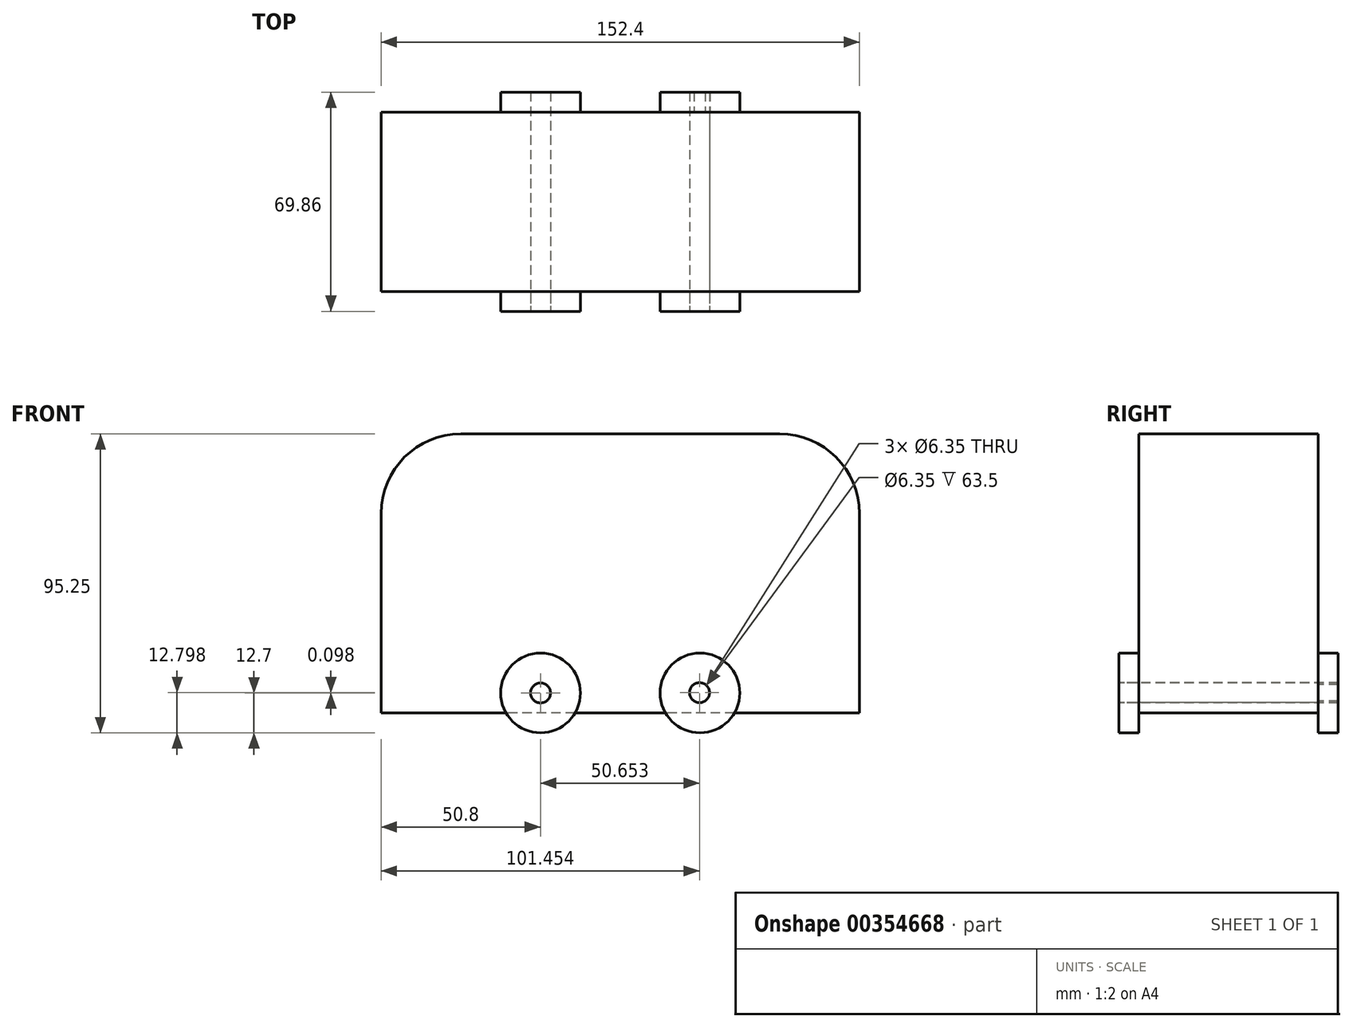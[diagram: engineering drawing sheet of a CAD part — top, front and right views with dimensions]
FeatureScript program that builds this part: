
annotation { "Feature Type Name" : "Feature", "Feature Type Description" : "" }
export const myFeature = defineFeature(function(context is Context, id is Id, definition is map)
    precondition{}
    {
        {
            var Q0;
            Q0=qCreatedBy(makeId("Front.planeOp"),FACE);
            var sketch = newSketch(context, id + "F0", { "sketchPlane" : qUnion([Q0])});
            skLineSegment(sketch, "E0.bottom", {"start": v(76.2, -44.45) * mm, "end": v(-76.2, -44.45) * mm});
            skLineSegment(sketch, "E0.top", {"start": v(50.8, 44.45) * mm, "end": v(-50.8, 44.45) * mm});
            skLineSegment(sketch, "E0.left", {"start": v(76.2, -44.45) * mm, "end": v(76.2, 19.05) * mm});
            skLineSegment(sketch, "E0.right", {"start": v(-76.2, -44.45) * mm, "end": v(-76.2, 19.05) * mm});
            skPoint(sketch, "E0.middle", {"position": v(0, 0) * mm});
            skPoint(sketch, "E1.visualSharp", {"position": v(-76.2, 44.45) * mm});
            skArc(sketch, "E1.filletArc", {"start": v(-50.8, 44.45) * mm, "mid": v(-68.76, 37.01) * mm, "end": v(-76.2, 19.05) * mm});
            skPoint(sketch, "E2.visualSharp", {"position": v(76.2, 44.45) * mm});
            skArc(sketch, "E2.filletArc", {"start": v(76.2, 19.05) * mm, "mid": v(68.76, 37.01) * mm, "end": v(50.8, 44.45) * mm});
            skSolve(sketch);
        }
        {
            var Q0;
            Q0=makeQuery(id+"F0.imprint","IMPRINT",FACE,{"disambiguationData":[TD([[makeQuery(id+"F0.imprint","IMPRINT",EDGE,{"derivedFrom":sQuery(id+"F0.wireOp",EDGE,"E0.bottom")}),-1.0]])]});
            extrude(context, id + "F1", {"entities" : qUnion([Q0]), "endBound" : BoundingType.SYMMETRIC, "depth" : 57.15 * mm});
        }
        {
            var Q0;
            Q0=makeQuery(id+"F1.opExtrude","CAP_FACE",FACE,{"disambiguationData":[OSD([sQuery(id+"F0.wireOp",EDGE,"E0.bottom"),sQuery(id+"F0.wireOp",EDGE,"E0.top"),sQuery(id+"F0.wireOp",EDGE,"E0.left"),sQuery(id+"F0.wireOp",EDGE,"E0.right")])],"isStart":false});
            var sketch = newSketch(context, id + "F2", { "sketchPlane" : qUnion([Q0])});
            skCircle(sketch, "E3", {"center": v(25.4, -38.1) * mm, "radius": 12.7 * mm});
            skCircle(sketch, "E4", {"center": v(-25.4, -38.1) * mm, "radius": 12.7 * mm});
            skSolve(sketch);
        }
        {
            var Q0;
            {var subQ0=sQuery(id+"F2.wireOp",EDGE,"E4");var subQ1=makeQuery(id+"F1.opExtrude","CAP_EDGE",EDGE,{"disambiguationData":[OSD([sQuery(id+"F0.wireOp",EDGE,"E0.bottom")])],"isStart":false});var subQ2=makeQuery(id+"F2.imprint","INTERSECT",VERTEX,{"disambiguationData":[OD(0.0)],"derivedFrom":[subQ1,subQ0]});Q0=makeQuery(id+"F2.imprint","IMPRINT",FACE,{"disambiguationData":[TD([[makeQuery(id+"F2.imprint","IMPRINT",EDGE,{"disambiguationData":[TD([[subQ2,1.0]])],"derivedFrom":subQ0}),1.0]])]});}
            var Q1;
            {var subQ0=sQuery(id+"F2.wireOp",EDGE,"E3");var subQ1=makeQuery(id+"F1.opExtrude","CAP_EDGE",EDGE,{"disambiguationData":[OSD([sQuery(id+"F0.wireOp",EDGE,"E0.bottom")])],"isStart":false});var subQ2=makeQuery(id+"F2.imprint","INTERSECT",VERTEX,{"disambiguationData":[OD(0.0)],"derivedFrom":[subQ1,subQ0]});Q1=makeQuery(id+"F2.imprint","IMPRINT",FACE,{"disambiguationData":[TD([[makeQuery(id+"F2.imprint","IMPRINT",EDGE,{"disambiguationData":[TD([[subQ2,-1.0]])],"derivedFrom":subQ0}),1.0]])]});}
            var Q2;
            {var subQ0=sQuery(id+"F2.wireOp",EDGE,"E4");var subQ1=makeQuery(id+"F1.opExtrude","CAP_EDGE",EDGE,{"disambiguationData":[OSD([sQuery(id+"F0.wireOp",EDGE,"E0.bottom")])],"isStart":false});var subQ2=makeQuery(id+"F2.imprint","INTERSECT",VERTEX,{"disambiguationData":[OD(0.0)],"derivedFrom":[subQ1,subQ0]});Q2=makeQuery(id+"F2.imprint","IMPRINT",FACE,{"disambiguationData":[TD([[makeQuery(id+"F2.imprint","IMPRINT",EDGE,{"disambiguationData":[TD([[subQ2,-1.0]])],"derivedFrom":subQ0}),1.0]])]});}
            var Q3;
            {var subQ0=sQuery(id+"F2.wireOp",EDGE,"E3");var subQ1=makeQuery(id+"F1.opExtrude","CAP_EDGE",EDGE,{"disambiguationData":[OSD([sQuery(id+"F0.wireOp",EDGE,"E0.bottom")])],"isStart":false});var subQ2=makeQuery(id+"F2.imprint","INTERSECT",VERTEX,{"disambiguationData":[OD(0.0)],"derivedFrom":[subQ1,subQ0]});Q3=makeQuery(id+"F2.imprint","IMPRINT",FACE,{"disambiguationData":[TD([[makeQuery(id+"F2.imprint","IMPRINT",EDGE,{"disambiguationData":[TD([[subQ2,1.0]])],"derivedFrom":subQ0}),1.0]])]});}
            var Q4;
            Q4=sQuery(id+"F2.wireOp",EDGE,"E3");
            var Q5;
            Q5=sQuery(id+"F2.wireOp",EDGE,"E4");
            extrude(context, id + "F3", {"entities" : qUnion([Q0, Q1, Q2, Q3]), "surfaceEntities" : qUnion([Q4, Q5]), "depth" : 6.35 * mm});
        }
        {
            var Q0;
            Q0=makeQuery(id+"F1.opExtrude","CAP_FACE",FACE,{"disambiguationData":[OSD([sQuery(id+"F0.wireOp",EDGE,"E0.bottom"),sQuery(id+"F0.wireOp",EDGE,"E0.top"),sQuery(id+"F0.wireOp",EDGE,"E0.left"),sQuery(id+"F0.wireOp",EDGE,"E0.right")])],"isStart":true});
            var sketch = newSketch(context, id + "F4", { "sketchPlane" : qUnion([Q0])});
            skCircle(sketch, "E5", {"center": v(-25.4, -38.1) * mm, "radius": 12.7 * mm});
            skCircle(sketch, "E6", {"center": v(25.4, -38.1) * mm, "radius": 12.7 * mm});
            skCircle(sketch, "E7", {"center": v(25.4, -38.1) * mm, "radius": 3.18 * mm});
            skCircle(sketch, "E8", {"center": v(-25.4, -38.1) * mm, "radius": 3.18 * mm});
            skSolve(sketch);
        }
        {
            var Q0;
            {var subQ0=sQuery(id+"F4.wireOp",EDGE,"E5");var subQ1=makeQuery(id+"F1.opExtrude","CAP_EDGE",EDGE,{"disambiguationData":[OSD([sQuery(id+"F0.wireOp",EDGE,"E0.bottom")])],"isStart":true});var subQ2=makeQuery(id+"F4.imprint","INTERSECT",VERTEX,{"disambiguationData":[OD(0.0)],"derivedFrom":[subQ1,subQ0]});Q0=makeQuery(id+"F4.imprint","IMPRINT",FACE,{"disambiguationData":[TD([[makeQuery(id+"F4.imprint","IMPRINT",EDGE,{"disambiguationData":[TD([[subQ2,-1.0]])],"derivedFrom":subQ0}),1.0]])]});}
            var Q1;
            {var subQ0=sQuery(id+"F4.wireOp",EDGE,"E6");var subQ1=makeQuery(id+"F1.opExtrude","CAP_EDGE",EDGE,{"disambiguationData":[OSD([sQuery(id+"F0.wireOp",EDGE,"E0.bottom")])],"isStart":true});var subQ2=makeQuery(id+"F4.imprint","INTERSECT",VERTEX,{"disambiguationData":[OD(0.0)],"derivedFrom":[subQ1,subQ0]});Q1=makeQuery(id+"F4.imprint","IMPRINT",FACE,{"disambiguationData":[TD([[makeQuery(id+"F4.imprint","IMPRINT",EDGE,{"disambiguationData":[TD([[subQ2,1.0]])],"derivedFrom":subQ0}),1.0]])]});}
            var Q2;
            {var subQ0=sQuery(id+"F4.wireOp",EDGE,"E6");var subQ1=makeQuery(id+"F1.opExtrude","CAP_EDGE",EDGE,{"disambiguationData":[OSD([sQuery(id+"F0.wireOp",EDGE,"E0.bottom")])],"isStart":true});var subQ2=makeQuery(id+"F4.imprint","INTERSECT",VERTEX,{"disambiguationData":[OD(0.0)],"derivedFrom":[subQ1,subQ0]});Q2=makeQuery(id+"F4.imprint","IMPRINT",FACE,{"disambiguationData":[TD([[makeQuery(id+"F4.imprint","IMPRINT",EDGE,{"disambiguationData":[TD([[subQ2,-1.0]])],"derivedFrom":subQ0}),1.0]])]});}
            var Q3;
            {var subQ0=sQuery(id+"F4.wireOp",EDGE,"E5");var subQ1=makeQuery(id+"F1.opExtrude","CAP_EDGE",EDGE,{"disambiguationData":[OSD([sQuery(id+"F0.wireOp",EDGE,"E0.bottom")])],"isStart":true});var subQ2=makeQuery(id+"F4.imprint","INTERSECT",VERTEX,{"disambiguationData":[OD(0.0)],"derivedFrom":[subQ1,subQ0]});Q3=makeQuery(id+"F4.imprint","IMPRINT",FACE,{"disambiguationData":[TD([[makeQuery(id+"F4.imprint","IMPRINT",EDGE,{"disambiguationData":[TD([[subQ2,1.0]])],"derivedFrom":subQ0}),1.0]])]});}
            var Q4;
            Q4 = qSketchRegion(id + "F6", true);
            extrude(context, id + "F5", {"entities" : qUnion([Q0, Q1, Q2, Q3, Q4]), "operationType" : NewBodyOperationType.ADD, "depth" : 6.35 * mm});
        }
        {
            var Q0;
            Q0=makeQuery(id+"F3.opExtrude","CAP_FACE",FACE,{"disambiguationData":[OSD([sQuery(id+"F2.wireOp",EDGE,"E4")])],"isStart":false});
            var sketch = newSketch(context, id + "F6", { "sketchPlane" : qUnion([Q0])});
            skCircle(sketch, "E9", {"center": v(-25.4, -38.1) * mm, "radius": 3.18 * mm});
            skCircle(sketch, "E10", {"center": v(25.25, -38) * mm, "radius": 3.18 * mm});
            skSolve(sketch);
        }
        {
            var Q0;
            Q0=makeQuery(id+"F6.imprint","IMPRINT",FACE,{"disambiguationData":[TD([[makeQuery(id+"F6.imprint","IMPRINT",EDGE,{"derivedFrom":sQuery(id+"F6.wireOp",EDGE,"E9")}),1.0]])]});
            var Q1;
            Q1=makeQuery(id+"F6.imprint","IMPRINT",FACE,{"disambiguationData":[TD([[makeQuery(id+"F6.imprint","IMPRINT",EDGE,{"derivedFrom":sQuery(id+"F6.wireOp",EDGE,"E10")}),1.0]])]});
            var Q2;
            Q2=makeQuery(id+"F4.imprint","IMPRINT",FACE,{"disambiguationData":[TD([[makeQuery(id+"F4.imprint","IMPRINT",EDGE,{"derivedFrom":sQuery(id+"F4.wireOp",EDGE,"E8")}),1.0]])]});
            var Q3;
            Q3=makeQuery(id+"F4.imprint","IMPRINT",FACE,{"disambiguationData":[TD([[makeQuery(id+"F4.imprint","IMPRINT",EDGE,{"derivedFrom":sQuery(id+"F4.wireOp",EDGE,"E7")}),1.0]])]});
            var Q4;
            Q4=makeQuery(id+"F5.opExtrude","CAP_FACE",FACE,{"disambiguationData":[OSD([sQuery(id+"F4.wireOp",EDGE,"E6"),sQuery(id+"F4.wireOp",EDGE,"E7")])],"isStart":false});
            var Q5;
            Q5=makeQuery(id+"F5.opExtrude","CAP_FACE",FACE,{"disambiguationData":[OSD([sQuery(id+"F4.wireOp",EDGE,"E5"),sQuery(id+"F4.wireOp",EDGE,"E8")])],"isStart":false});
            extrude(context, id + "F7", {"entities" : qUnion([Q0, Q1, Q2, Q3, Q4, Q5]), "operationType" : NewBodyOperationType.REMOVE, "endBound" : BoundingType.THROUGH_ALL, "oppositeDirection" : true, "depth" : 25.4 * mm});
        }
        {
            var Q0;
            Q0=makeQuery(id+"F6.imprint","IMPRINT",FACE,{"disambiguationData":[TD([[makeQuery(id+"F6.imprint","IMPRINT",EDGE,{"derivedFrom":sQuery(id+"F6.wireOp",EDGE,"E9")}),1.0]])]});
            var Q1;
            Q1=makeQuery(id+"F6.imprint","IMPRINT",FACE,{"disambiguationData":[TD([[makeQuery(id+"F6.imprint","IMPRINT",EDGE,{"derivedFrom":sQuery(id+"F6.wireOp",EDGE,"E10")}),1.0]])]});
            var Q2;
            Q2=sQuery(id+"F6.wireOp",EDGE,"E9");
            var Q3;
            Q3=sQuery(id+"F6.wireOp",EDGE,"E10");
            extrude(context, id + "F8", {"entities" : qUnion([Q0, Q1]), "surfaceEntities" : qUnion([Q2, Q3]), "oppositeDirection" : true, "depth" : 69.85 * mm});
        }
    });
